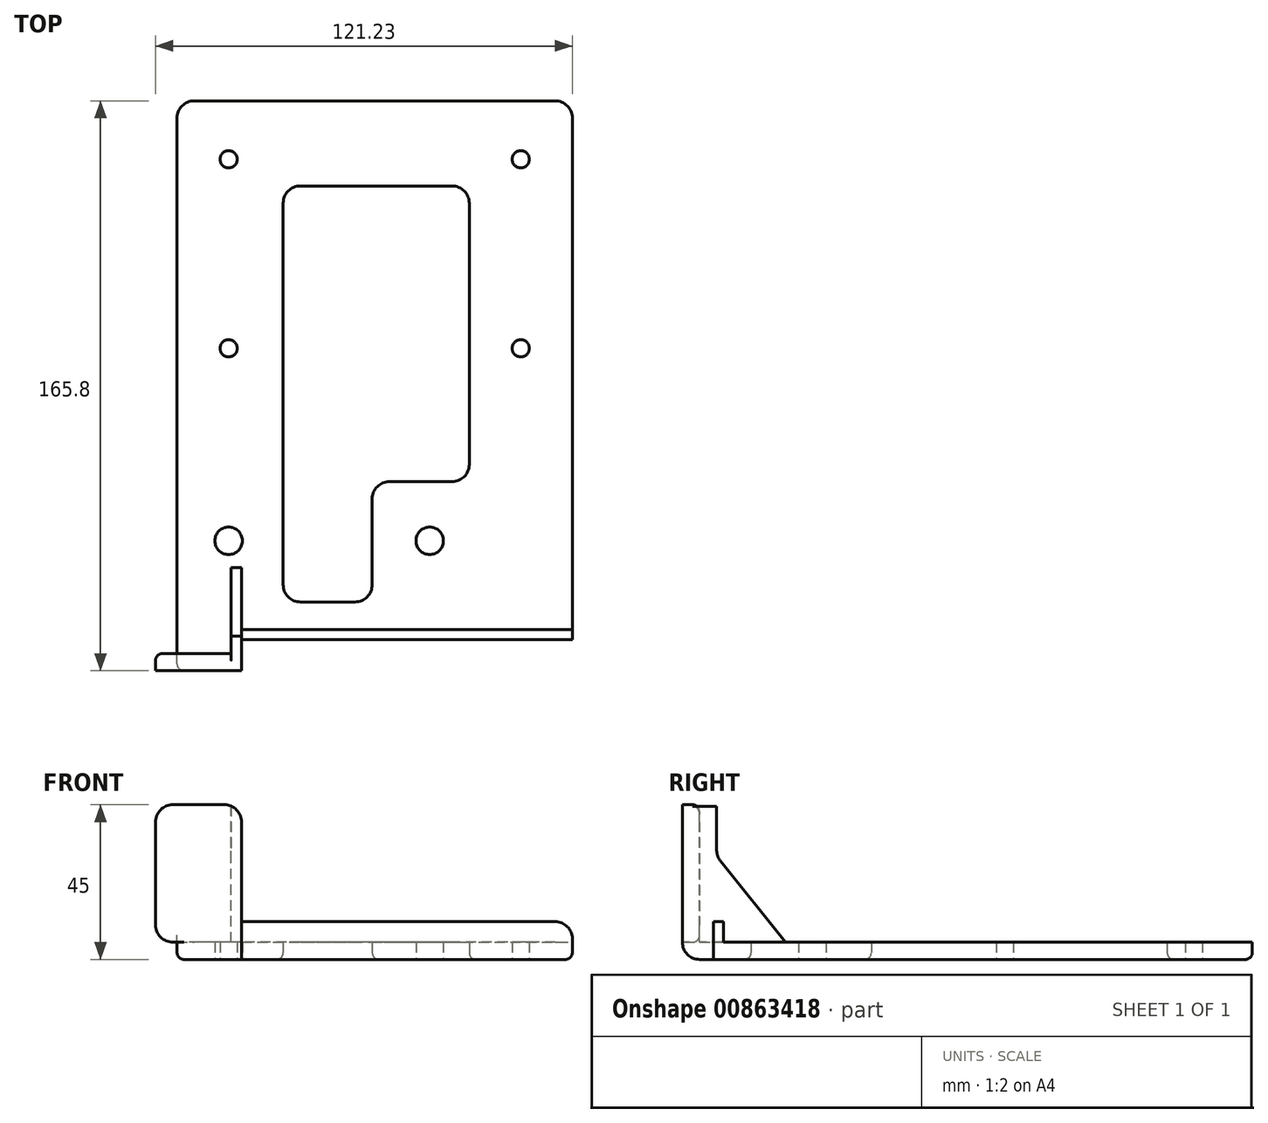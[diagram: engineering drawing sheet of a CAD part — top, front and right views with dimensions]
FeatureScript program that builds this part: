
annotation { "Feature Type Name" : "Feature", "Feature Type Description" : "" }
export const myFeature = defineFeature(function(context is Context, id is Id, definition is map)
    precondition{}
    {
        {
            var Q0;
            Q0=qCreatedBy(makeId("Top.planeOp"),FACE);
            var sketch = newSketch(context, id + "F0", { "sketchPlane" : qUnion([Q0])});
            skLineSegment(sketch, "E0.bottom", {"start": v(0, 0) * mm, "end": v(-115, 0) * mm});
            skLineSegment(sketch, "E0.top", {"start": v(0, 165.8) * mm, "end": v(-115, 165.8) * mm});
            skLineSegment(sketch, "E0.left", {"start": v(0, 0) * mm, "end": v(0, 165.8) * mm});
            skLineSegment(sketch, "E0.right", {"start": v(-115, 0) * mm, "end": v(-115, 165.8) * mm});
            skCircle(sketch, "E1", {"center": v(-41.5, 37.8) * mm, "radius": 4 * mm});
            skCircle(sketch, "E2", {"center": v(-100, 37.8) * mm, "radius": 4 * mm});
            skCircle(sketch, "E3", {"center": v(-100, 148.8) * mm, "radius": 2.5 * mm});
            skCircle(sketch, "E4", {"center": v(-100, 93.8) * mm, "radius": 2.5 * mm});
            skCircle(sketch, "E5", {"center": v(-15, 148.8) * mm, "radius": 2.5 * mm});
            skCircle(sketch, "E6", {"center": v(-15, 93.8) * mm, "radius": 2.5 * mm});
            skLineSegment(sketch, "E7", {"start": v(-30, 141.04) * mm, "end": v(-84.13, 141.04) * mm});
            skLineSegment(sketch, "E8", {"start": v(-84.13, 141.04) * mm, "end": v(-84.13, 20) * mm});
            skLineSegment(sketch, "E9", {"start": v(-84.13, 20) * mm, "end": v(-58.23, 20) * mm});
            skLineSegment(sketch, "E10", {"start": v(-58.23, 20) * mm, "end": v(-58.23, 55) * mm});
            skLineSegment(sketch, "E11", {"start": v(-58.23, 55) * mm, "end": v(-30, 55) * mm});
            skLineSegment(sketch, "E12", {"start": v(-30, 55) * mm, "end": v(-30, 141.04) * mm});
            skPoint(sketch, "E13.orphan", {"position": v(-35.31, 141.04) * mm});
            skSolve(sketch);
        }
        {
            var Q0;
            Q0=makeQuery(id+"F0.imprint","IMPRINT",FACE,{"disambiguationData":[TD([[makeQuery(id+"F0.imprint","IMPRINT",EDGE,{"derivedFrom":sQuery(id+"F0.wireOp",EDGE,"E0.bottom")}),-1.0]])]});
            extrude(context, id + "F1", {"entities" : qUnion([Q0]), "oppositeDirection" : true, "depth" : 5 * mm, "offsetDistance" : 25 * mm});
        }
        {
            var Q0;
            Q0=makeQuery(id+"F1.opExtrude","CAP_FACE",FACE,{"disambiguationData":[OSD([sQuery(id+"F0.wireOp",EDGE,"E0.bottom"),sQuery(id+"F0.wireOp",EDGE,"E0.top"),sQuery(id+"F0.wireOp",EDGE,"E0.left"),sQuery(id+"F0.wireOp",EDGE,"E0.right"),sQuery(id+"F0.wireOp",EDGE,"E1"),sQuery(id+"F0.wireOp",EDGE,"E2"),sQuery(id+"F0.wireOp",EDGE,"E3"),sQuery(id+"F0.wireOp",EDGE,"E4"),sQuery(id+"F0.wireOp",EDGE,"E5"),sQuery(id+"F0.wireOp",EDGE,"E6"),sQuery(id+"F0.wireOp",EDGE,"AMhIYsyM-ouOh-bC3b-tB5I-rpUGRMd0qDAw.bottom"),sQuery(id+"F0.wireOp",EDGE,"AMhIYsyM-ouOh-bC3b-tB5I-rpUGRMd0qDAw.top"),sQuery(id+"F0.wireOp",EDGE,"AMhIYsyM-ouOh-bC3b-tB5I-rpUGRMd0qDAw.left"),sQuery(id+"F0.wireOp",EDGE,"AMhIYsyM-ouOh-bC3b-tB5I-rpUGRMd0qDAw.right")])],"isStart":false});
            var sketch = newSketch(context, id + "F2", { "sketchPlane" : qUnion([Q0])});
            skLineSegment(sketch, "E14.bottom", {"start": v(-96.23, 0) * mm, "end": v(-121.23, 0) * mm});
            skLineSegment(sketch, "E14.top", {"start": v(-96.23, -5) * mm, "end": v(-121.23, -5) * mm});
            skLineSegment(sketch, "E14.left", {"start": v(-96.23, 0) * mm, "end": v(-96.23, -5) * mm});
            skLineSegment(sketch, "E14.right", {"start": v(-121.23, 0) * mm, "end": v(-121.23, -5) * mm});
            skSolve(sketch);
        }
        {
            var Q0;
            Q0=makeQuery(id+"F2.imprint","IMPRINT",FACE,{"disambiguationData":[TD([[makeQuery(id+"F2.imprint","IMPRINT",EDGE,{"derivedFrom":sQuery(id+"F2.wireOp",EDGE,"E14.bottom")}),1.0]])]});
            extrude(context, id + "F3", {"entities" : qUnion([Q0]), "operationType" : NewBodyOperationType.ADD, "depth" : 40 * mm, "offsetDistance" : 25 * mm});
        }
        {
            var Q0;
            Q0=makeQuery(id+"F3.opExtrude","SWEPT_FACE",FACE,{"disambiguationData":[OSD([sQuery(id+"F2.wireOp",EDGE,"E14.top")])]});
            var sketch = newSketch(context, id + "F4", { "sketchPlane" : qUnion([Q0])});
            skLineSegment(sketch, "E15.bottom", {"start": v(96.23, -5) * mm, "end": v(99.23, -5) * mm});
            skLineSegment(sketch, "E15.top", {"start": v(96.23, -30) * mm, "end": v(99.23, -30) * mm});
            skLineSegment(sketch, "E15.left", {"start": v(96.23, -5) * mm, "end": v(96.23, -30) * mm});
            skLineSegment(sketch, "E15.right", {"start": v(99.23, -5) * mm, "end": v(99.23, -30) * mm});
            skLineSegment(sketch, "E16.bottom", {"start": v(186.23, -3.5) * mm, "end": v(183.23, -3.5) * mm});
            skLineSegment(sketch, "E16.top", {"start": v(186.23, -28.5) * mm, "end": v(183.23, -28.5) * mm});
            skLineSegment(sketch, "E16.left", {"start": v(186.23, -3.5) * mm, "end": v(186.23, -28.5) * mm});
            skLineSegment(sketch, "E16.right", {"start": v(183.23, -3.5) * mm, "end": v(183.23, -28.5) * mm});
            skPoint(sketch, "E17", {"position": v(186.23, -3.5) * mm});
            skSolve(sketch);
        }
        {
            var Q0;
            Q0=makeQuery(id+"F4.imprint","IMPRINT",FACE,{"disambiguationData":[TD([[makeQuery(id+"F4.imprint","IMPRINT",EDGE,{"derivedFrom":sQuery(id+"F4.wireOp",EDGE,"E15.bottom")}),-1.0]])]});
            var Q1;
            Q1=makeQuery(id+"F4.imprint","IMPRINT",FACE,{"disambiguationData":[TD([[makeQuery(id+"F4.imprint","IMPRINT",EDGE,{"derivedFrom":sQuery(id+"F4.wireOp",EDGE,"E16.bottom")}),-1.0]])]});
            extrude(context, id + "F5", {"entities" : qUnion([Q0, Q1]), "operationType" : NewBodyOperationType.ADD, "depth" : 25 * mm, "offsetDistance" : 25 * mm});
        }
        {
            var Q0;
            Q0=makeQuery(id+"F0.imprint","IMPRINT",FACE,{"disambiguationData":[TD([[makeQuery(id+"F0.imprint","IMPRINT",EDGE,{"derivedFrom":sQuery(id+"F0.wireOp",EDGE,"E0.bottom")}),-1.0]])]});
            var sketch = newSketch(context, id + "F6", { "sketchPlane" : qUnion([Q0])});
            skLineSegment(sketch, "E18.top", {"start": v(-115.06, 0) * mm, "end": v(-110.06, 0) * mm});
            skLineSegment(sketch, "E18.left", {"start": v(-115.06, 165.8) * mm, "end": v(-115.06, 0) * mm});
            skLineSegment(sketch, "E18.right", {"start": v(-110.06, 165.8) * mm, "end": v(-110.06, 0) * mm});
            skLineSegment(sketch, "E19.bottom", {"start": v(0, 165.8) * mm, "end": v(-5, 165.8) * mm});
            skLineSegment(sketch, "E19.top", {"start": v(0, 0) * mm, "end": v(-5, 0) * mm});
            skLineSegment(sketch, "E19.left", {"start": v(0, 165.8) * mm, "end": v(0, 0) * mm});
            skLineSegment(sketch, "E19.right", {"start": v(-5, 165.8) * mm, "end": v(-5, 0) * mm});
            skLineSegment(sketch, "E20.top", {"start": v(-115.06, 165.8) * mm, "end": v(-115.06, 165.8) * mm});
            skLineSegment(sketch, "E21", {"start": v(-115.06, 165.8) * mm, "end": v(-110.06, 165.8) * mm});
            skSolve(sketch);
        }
        {
            var Q0;
            Q0=makeQuery(id+"F1.opExtrude","SWEPT_BODY",BODY,{"disambiguationData":[OSD([sQuery(id+"F0.wireOp",EDGE,"E0.bottom"),sQuery(id+"F0.wireOp",EDGE,"E0.top"),sQuery(id+"F0.wireOp",EDGE,"E0.left"),sQuery(id+"F0.wireOp",EDGE,"E0.right"),sQuery(id+"F0.wireOp",EDGE,"E1"),sQuery(id+"F0.wireOp",EDGE,"E2"),sQuery(id+"F0.wireOp",EDGE,"E3"),sQuery(id+"F0.wireOp",EDGE,"E4"),sQuery(id+"F0.wireOp",EDGE,"E5"),sQuery(id+"F0.wireOp",EDGE,"E6"),sQuery(id+"F0.wireOp",EDGE,"E7"),sQuery(id+"F0.wireOp",EDGE,"E8"),sQuery(id+"F0.wireOp",EDGE,"E9"),sQuery(id+"F0.wireOp",EDGE,"E10"),sQuery(id+"F0.wireOp",EDGE,"E11"),sQuery(id+"F0.wireOp",EDGE,"E12")])]});
            var Q1;
            Q1=makeQuery(id+"F6.imprint","IMPRINT",FACE,{"disambiguationData":[TD([[makeQuery(id+"F6.imprint","IMPRINT",EDGE,{"derivedFrom":sQuery(id+"F6.wireOp",EDGE,"E19.bottom")}),1.0]])]});
            mirror(context, id + "F7", {"entities" : qUnion([Q0]), "mirrorPlane" : qUnion([Q1])});
        }
        {
            var Q0;
            Q0=makeQuery(id+"F1.opExtrude","SWEPT_BODY",BODY,{"disambiguationData":[OSD([sQuery(id+"F0.wireOp",EDGE,"E0.bottom"),sQuery(id+"F0.wireOp",EDGE,"E0.top"),sQuery(id+"F0.wireOp",EDGE,"E0.left"),sQuery(id+"F0.wireOp",EDGE,"E0.right"),sQuery(id+"F0.wireOp",EDGE,"E1"),sQuery(id+"F0.wireOp",EDGE,"E2"),sQuery(id+"F0.wireOp",EDGE,"E3"),sQuery(id+"F0.wireOp",EDGE,"E4"),sQuery(id+"F0.wireOp",EDGE,"E5"),sQuery(id+"F0.wireOp",EDGE,"E6"),sQuery(id+"F0.wireOp",EDGE,"E7"),sQuery(id+"F0.wireOp",EDGE,"E8"),sQuery(id+"F0.wireOp",EDGE,"E9"),sQuery(id+"F0.wireOp",EDGE,"E10"),sQuery(id+"F0.wireOp",EDGE,"E11"),sQuery(id+"F0.wireOp",EDGE,"E12")])]});
            deleteBodies(context, id + "F8", {"entities" : qUnion([Q0])});
        }
        {
            var Q0;
            Q0=makeQuery(id+"F7.opPattern","COPY",FACE,{"derivedFrom":makeQuery(id+"F5.opExtrude","SWEPT_FACE",FACE,{"disambiguationData":[OSD([sQuery(id+"F4.wireOp",EDGE,"E15.top")])]}),"instanceName":"1"});
            var sketch = newSketch(context, id + "F9", { "sketchPlane" : qUnion([Q0])});
            skLineSegment(sketch, "E22.bottom", {"start": v(-96.23, 5) * mm, "end": v(-99.23, 5) * mm});
            skLineSegment(sketch, "E22.top", {"start": v(-96.23, 10) * mm, "end": v(-99.23, 10) * mm});
            skLineSegment(sketch, "E22.left", {"start": v(-96.23, 5) * mm, "end": v(-96.23, 10) * mm});
            skLineSegment(sketch, "E22.right", {"start": v(-99.23, 5) * mm, "end": v(-99.23, 10) * mm});
            skSolve(sketch);
        }
        {
            var Q0;
            Q0=makeQuery(id+"F9.imprint","IMPRINT",FACE,{"disambiguationData":[TD([[makeQuery(id+"F9.imprint","IMPRINT",EDGE,{"derivedFrom":sQuery(id+"F9.wireOp",EDGE,"E22.bottom")}),-1.0]])]});
            extrude(context, id + "F10", {"entities" : qUnion([Q0]), "operationType" : NewBodyOperationType.ADD, "depth" : 14.58 * mm, "offsetDistance" : 25 * mm});
        }
        {
            var Q0;
            Q0=makeQuery(id+"F10.boolean.opBoolean","MERGE",FACE,{"derivedFrom":[makeQuery(id+"F7.opPattern","COPY",FACE,{"derivedFrom":makeQuery(id+"F5.opExtrude","SWEPT_FACE",FACE,{"disambiguationData":[OSD([sQuery(id+"F4.wireOp",EDGE,"E15.right")])]}),"instanceName":"1"}),makeQuery(id+"F10.opExtrude","SWEPT_FACE",FACE,{"disambiguationData":[OSD([sQuery(id+"F9.wireOp",EDGE,"E22.right")])]})]});
            var sketch = newSketch(context, id + "F11", { "sketchPlane" : qUnion([Q0])});
            skLineSegment(sketch, "E23", {"start": v(-30, 5) * mm, "end": v(-10, 30) * mm});
            skSolve(sketch);
        }
        {
            var Q0;
            Q0=makeQuery(id+"F11.imprint","IMPRINT",FACE,{"disambiguationData":[TD([[makeQuery(id+"F11.imprint","IMPRINT",EDGE,{"derivedFrom":sQuery(id+"F11.wireOp",EDGE,"E23")}),1.0]])]});
            extrude(context, id + "F12", {"entities" : qUnion([Q0]), "operationType" : NewBodyOperationType.REMOVE, "endBound" : BoundingType.UP_TO_NEXT, "oppositeDirection" : true, "depth" : 25 * mm, "offsetDistance" : 25 * mm});
        }
        {
            var Q0;
            Q0=makeQuery(id+"F7.opPattern","COPY",FACE,{"derivedFrom":makeQuery(id+"F1.opExtrude","CAP_FACE",FACE,{"disambiguationData":[OSD([sQuery(id+"F0.wireOp",EDGE,"E0.bottom"),sQuery(id+"F0.wireOp",EDGE,"E0.top"),sQuery(id+"F0.wireOp",EDGE,"E0.left"),sQuery(id+"F0.wireOp",EDGE,"E0.right"),sQuery(id+"F0.wireOp",EDGE,"E1"),sQuery(id+"F0.wireOp",EDGE,"E2"),sQuery(id+"F0.wireOp",EDGE,"E3"),sQuery(id+"F0.wireOp",EDGE,"E4"),sQuery(id+"F0.wireOp",EDGE,"E5"),sQuery(id+"F0.wireOp",EDGE,"E6"),sQuery(id+"F0.wireOp",EDGE,"E7"),sQuery(id+"F0.wireOp",EDGE,"E8"),sQuery(id+"F0.wireOp",EDGE,"E9"),sQuery(id+"F0.wireOp",EDGE,"E10"),sQuery(id+"F0.wireOp",EDGE,"E11"),sQuery(id+"F0.wireOp",EDGE,"E12")])],"isStart":false}),"instanceName":"1"});
            var sketch = newSketch(context, id + "F13", { "sketchPlane" : qUnion([Q0])});
            skLineSegment(sketch, "E24.bottom", {"start": v(-96.23, 0) * mm, "end": v(0, 0) * mm});
            skLineSegment(sketch, "E24.top", {"start": v(-96.23, 0) * mm, "end": v(0, 0) * mm});
            skLineSegment(sketch, "E24.left", {"start": v(-96.23, 0) * mm, "end": v(-96.23, 0) * mm});
            skLineSegment(sketch, "E24.right", {"start": v(0, 0) * mm, "end": v(0, 0) * mm});
            skLineSegment(sketch, "E25.top", {"start": v(-96.23, 9) * mm, "end": v(0, 9) * mm});
            skLineSegment(sketch, "E25.left", {"start": v(-96.23, 0) * mm, "end": v(-96.23, 9) * mm});
            skLineSegment(sketch, "E25.right", {"start": v(0, 0) * mm, "end": v(0, 9) * mm});
            skSolve(sketch);
        }
        {
            var Q0;
            Q0=makeQuery(id+"F13.imprint","IMPRINT",FACE,{"disambiguationData":[TD([[makeQuery(id+"F13.imprint","IMPRINT",EDGE,{"derivedFrom":sQuery(id+"F13.wireOp",EDGE,"E24.bottom")}),-1.0]])]});
            extrude(context, id + "F14", {"entities" : qUnion([Q0]), "operationType" : NewBodyOperationType.REMOVE, "endBound" : BoundingType.UP_TO_NEXT, "oppositeDirection" : true, "depth" : 25 * mm, "offsetDistance" : 25 * mm});
        }
        {
            var Q0;
            Q0=makeQuery(id+"F7.opPattern","COPY",FACE,{"derivedFrom":makeQuery(id+"F1.opExtrude","CAP_FACE",FACE,{"disambiguationData":[OSD([sQuery(id+"F0.wireOp",EDGE,"E0.bottom"),sQuery(id+"F0.wireOp",EDGE,"E0.top"),sQuery(id+"F0.wireOp",EDGE,"E0.left"),sQuery(id+"F0.wireOp",EDGE,"E0.right"),sQuery(id+"F0.wireOp",EDGE,"E1"),sQuery(id+"F0.wireOp",EDGE,"E2"),sQuery(id+"F0.wireOp",EDGE,"E3"),sQuery(id+"F0.wireOp",EDGE,"E4"),sQuery(id+"F0.wireOp",EDGE,"E5"),sQuery(id+"F0.wireOp",EDGE,"E6"),sQuery(id+"F0.wireOp",EDGE,"E7"),sQuery(id+"F0.wireOp",EDGE,"E8"),sQuery(id+"F0.wireOp",EDGE,"E9"),sQuery(id+"F0.wireOp",EDGE,"E10"),sQuery(id+"F0.wireOp",EDGE,"E11"),sQuery(id+"F0.wireOp",EDGE,"E12")])],"isStart":false}),"instanceName":"1"});
            var sketch = newSketch(context, id + "F15", { "sketchPlane" : qUnion([Q0])});
            skLineSegment(sketch, "E26.bottom", {"start": v(-96.23, 9) * mm, "end": v(0, 9) * mm});
            skLineSegment(sketch, "E26.top", {"start": v(-96.23, 12) * mm, "end": v(0, 12) * mm});
            skLineSegment(sketch, "E26.left", {"start": v(-96.23, 9) * mm, "end": v(-96.23, 12) * mm});
            skLineSegment(sketch, "E26.right", {"start": v(0, 9) * mm, "end": v(0, 12) * mm});
            skSolve(sketch);
        }
        {
            var Q0;
            Q0=makeQuery(id+"F15.imprint","IMPRINT",FACE,{"disambiguationData":[TD([[makeQuery(id+"F15.imprint","IMPRINT",EDGE,{"derivedFrom":sQuery(id+"F15.wireOp",EDGE,"E26.bottom")}),1.0]])]});
            extrude(context, id + "F16", {"entities" : qUnion([Q0]), "operationType" : NewBodyOperationType.ADD, "depth" : 6 * mm, "offsetDistance" : 25 * mm});
        }
        {
            var Q0;
            {var subQ0=sQuery(id+"F9.wireOp",EDGE,"E22.top");Q0=makeQuery(id+"F12.boolean.opBoolean","MERGE",EDGE,{"derivedFrom":[makeQuery(id+"F10.opExtrude","CAP_EDGE",EDGE,{"disambiguationData":[OSD([subQ0])],"isStart":true})],"fromTools":[makeQuery(id+"F12.opExtrude","SWEPT_EDGE",EDGE,{"disambiguationData":[OSD([sQuery(id+"F4.wireOp",EDGE,"E15.top"),sQuery(id+"F4.wireOp",EDGE,"E15.right"),subQ0,sQuery(id+"F9.wireOp",EDGE,"E22.right"),sQuery(id+"F11.wireOp",EDGE,"E23")])]})]});}
            var Q1;
            Q1=makeQuery(id+"F7.opPattern","COPY",EDGE,{"derivedFrom":makeQuery(id+"F1.opExtrude","CAP_EDGE",EDGE,{"disambiguationData":[OSD([sQuery(id+"F0.wireOp",EDGE,"E0.bottom")])],"isStart":true}),"instanceName":"1"});
            var Q2;
            Q2=makeQuery(id+"F7.opPattern","COPY",EDGE,{"derivedFrom":makeQuery(id+"F3.opExtrude","CAP_EDGE",EDGE,{"disambiguationData":[OSD([sQuery(id+"F2.wireOp",EDGE,"E14.left")])],"isStart":false}),"instanceName":"1"});
            var Q3;
            Q3=makeQuery(id+"F7.opPattern","COPY",EDGE,{"derivedFrom":makeQuery(id+"F3.opExtrude","CAP_EDGE",EDGE,{"disambiguationData":[OSD([sQuery(id+"F2.wireOp",EDGE,"E14.right")])],"isStart":false}),"instanceName":"1"});
            var Q4;
            Q4=makeQuery(id+"F7.opPattern","COPY",EDGE,{"derivedFrom":makeQuery(id+"F3.opExtrude","CAP_EDGE",EDGE,{"disambiguationData":[OSD([sQuery(id+"F2.wireOp",EDGE,"E14.right")])],"isStart":true}),"instanceName":"1"});
            var Q5;
            Q5=makeQuery(id+"F7.opPattern","COPY",EDGE,{"derivedFrom":makeQuery(id+"F1.opExtrude","SWEPT_EDGE",EDGE,{"disambiguationData":[OSD([sQuery(id+"F0.wireOp",EDGE,"E0.top"),sQuery(id+"F0.wireOp",EDGE,"E0.right")])]}),"instanceName":"1"});
            var Q6;
            Q6=makeQuery(id+"F7.opPattern","COPY",EDGE,{"derivedFrom":makeQuery(id+"F1.opExtrude","SWEPT_EDGE",EDGE,{"disambiguationData":[OSD([sQuery(id+"F0.wireOp",EDGE,"E0.top"),sQuery(id+"F0.wireOp",EDGE,"E0.left")])]}),"instanceName":"1"});
            var Q7;
            Q7=makeQuery(id+"F16.opExtrude","CAP_EDGE",EDGE,{"disambiguationData":[OSD([sQuery(id+"F15.wireOp",EDGE,"E26.right")])],"isStart":false});
            var Q8;
            Q8=makeQuery(id+"F7.opPattern","COPY",EDGE,{"derivedFrom":makeQuery(id+"F1.opExtrude","SWEPT_EDGE",EDGE,{"disambiguationData":[OSD([sQuery(id+"F0.wireOp",EDGE,"E10"),sQuery(id+"F0.wireOp",EDGE,"E11")])]}),"instanceName":"1"});
            var Q9;
            Q9=makeQuery(id+"F7.opPattern","COPY",EDGE,{"derivedFrom":makeQuery(id+"F1.opExtrude","SWEPT_EDGE",EDGE,{"disambiguationData":[OSD([sQuery(id+"F0.wireOp",EDGE,"E11"),sQuery(id+"F0.wireOp",EDGE,"E12")])]}),"instanceName":"1"});
            var Q10;
            Q10=makeQuery(id+"F7.opPattern","COPY",EDGE,{"derivedFrom":makeQuery(id+"F1.opExtrude","SWEPT_EDGE",EDGE,{"disambiguationData":[OSD([sQuery(id+"F0.wireOp",EDGE,"E9"),sQuery(id+"F0.wireOp",EDGE,"E10")])]}),"instanceName":"1"});
            var Q11;
            Q11=makeQuery(id+"F7.opPattern","COPY",EDGE,{"derivedFrom":makeQuery(id+"F1.opExtrude","SWEPT_EDGE",EDGE,{"disambiguationData":[OSD([sQuery(id+"F0.wireOp",EDGE,"E8"),sQuery(id+"F0.wireOp",EDGE,"E9")])]}),"instanceName":"1"});
            var Q12;
            Q12=makeQuery(id+"F7.opPattern","COPY",EDGE,{"derivedFrom":makeQuery(id+"F1.opExtrude","SWEPT_EDGE",EDGE,{"disambiguationData":[OSD([sQuery(id+"F0.wireOp",EDGE,"E7"),sQuery(id+"F0.wireOp",EDGE,"E12")])]}),"instanceName":"1"});
            var Q13;
            Q13=makeQuery(id+"F7.opPattern","COPY",EDGE,{"derivedFrom":makeQuery(id+"F1.opExtrude","SWEPT_EDGE",EDGE,{"disambiguationData":[OSD([sQuery(id+"F0.wireOp",EDGE,"E7"),sQuery(id+"F0.wireOp",EDGE,"E8")])]}),"instanceName":"1"});
            var Q14;
            Q14=makeQuery(id+"F14.boolean.opBoolean","COPY",EDGE,{"derivedFrom":makeQuery(id+"F14.opExtrude","CAP_EDGE",EDGE,{"disambiguationData":[OSD([sQuery(id+"F13.wireOp",EDGE,"E25.top")])],"isStart":false})});
            fillet(context, id + "F17", {"entities" : qUnion([Q0, Q1, Q2, Q3, Q4, Q5, Q6, Q7, Q8, Q9, Q10, Q11, Q12, Q13, Q14]), "radius" : 5 * mm, "tangentPropagation" : true, "allowEdgeOverflow" : false});
        }
        {
            var Q0;
            Q0=makeQuery(id+"F17.opFillet","BLEND_EDGE",EDGE,{"blendedFrom":[makeQuery(id+"F7.opPattern","COPY",EDGE,{"derivedFrom":makeQuery(id+"F1.opExtrude","CAP_EDGE",EDGE,{"disambiguationData":[OSD([sQuery(id+"F0.wireOp",EDGE,"E0.bottom")])],"isStart":true}),"instanceName":"1"}),makeQuery(id+"F16.boolean.opBoolean","MERGE",FACE,{"derivedFrom":[makeQuery(id+"F14.boolean.opBoolean","COPY",FACE,{"derivedFrom":makeQuery(id+"F14.opExtrude","SWEPT_FACE",FACE,{"disambiguationData":[OSD([sQuery(id+"F13.wireOp",EDGE,"E25.top")])]})}),makeQuery(id+"F16.opExtrude","SWEPT_FACE",FACE,{"disambiguationData":[OSD([sQuery(id+"F15.wireOp",EDGE,"E26.bottom")])]})]})],"blendedInto":[makeQuery(id+"F16.boolean.opBoolean","MERGE",FACE,{"derivedFrom":[makeQuery(id+"F14.boolean.opBoolean","COPY",FACE,{"derivedFrom":makeQuery(id+"F14.opExtrude","SWEPT_FACE",FACE,{"disambiguationData":[OSD([sQuery(id+"F13.wireOp",EDGE,"E25.top")])]})}),makeQuery(id+"F16.opExtrude","SWEPT_FACE",FACE,{"disambiguationData":[OSD([sQuery(id+"F15.wireOp",EDGE,"E26.bottom")])]})]})]});
            var Q1;
            Q1=makeQuery(id+"F16.opExtrude","CAP_EDGE",EDGE,{"disambiguationData":[OSD([sQuery(id+"F15.wireOp",EDGE,"E26.top")])],"isStart":true});
            var Q2;
            {var subQ0=sQuery(id+"F2.wireOp",EDGE,"E14.top");Q2=makeQuery(id+"F7.opPattern","COPY",EDGE,{"derivedFrom":makeQuery(id+"F3.boolean.opBoolean","SPLIT",EDGE,{"disambiguationData":[topologyDisambiguationEdgeConnected([makeQuery(id+"F1.opExtrude","CAP_FACE",FACE,{"disambiguationData":[OSD([sQuery(id+"F0.wireOp",EDGE,"E0.bottom"),sQuery(id+"F0.wireOp",EDGE,"E0.top"),sQuery(id+"F0.wireOp",EDGE,"E0.left"),sQuery(id+"F0.wireOp",EDGE,"E0.right"),sQuery(id+"F0.wireOp",EDGE,"E1"),sQuery(id+"F0.wireOp",EDGE,"E2"),sQuery(id+"F0.wireOp",EDGE,"E3"),sQuery(id+"F0.wireOp",EDGE,"E4"),sQuery(id+"F0.wireOp",EDGE,"E5"),sQuery(id+"F0.wireOp",EDGE,"E6"),sQuery(id+"F0.wireOp",EDGE,"E7"),sQuery(id+"F0.wireOp",EDGE,"E8"),sQuery(id+"F0.wireOp",EDGE,"E9"),sQuery(id+"F0.wireOp",EDGE,"E10"),sQuery(id+"F0.wireOp",EDGE,"E11"),sQuery(id+"F0.wireOp",EDGE,"E12")])],"isStart":false})])],"derivedFrom":makeQuery(id+"F3.opExtrude","CAP_EDGE",EDGE,{"disambiguationData":[OSD([subQ0])],"isStart":true})}),"instanceName":"1"});}
            var Q3;
            Q3=makeQuery(id+"F7.opPattern","COPY",EDGE,{"derivedFrom":makeQuery(id+"F1.opExtrude","CAP_EDGE",EDGE,{"disambiguationData":[OSD([sQuery(id+"F0.wireOp",EDGE,"E0.left")])],"isStart":true}),"instanceName":"1"});
            var Q4;
            Q4=makeQuery(id+"F7.opPattern","COPY",EDGE,{"derivedFrom":makeQuery(id+"F1.opExtrude","CAP_EDGE",EDGE,{"disambiguationData":[OSD([sQuery(id+"F0.wireOp",EDGE,"E12")])],"isStart":true}),"instanceName":"1"});
            fillet(context, id + "F18", {"entities" : qUnion([Q0, Q1, Q2, Q3, Q4]), "radius" : 2 * mm, "tangentPropagation" : true, "allowEdgeOverflow" : false});
        }
    });
